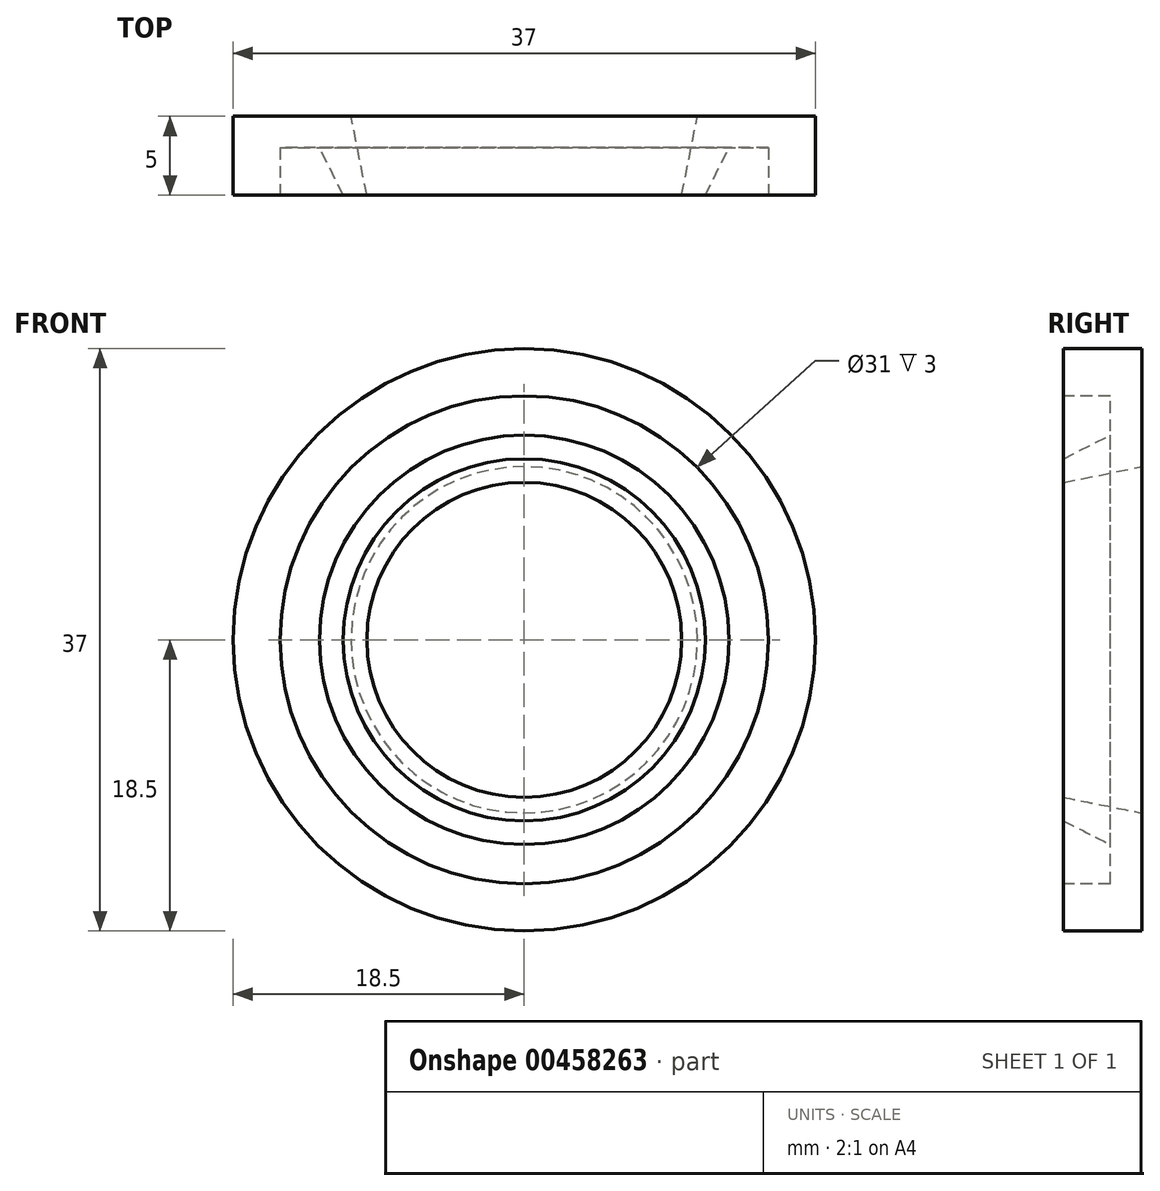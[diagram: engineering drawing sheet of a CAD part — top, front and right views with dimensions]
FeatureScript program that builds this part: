
annotation { "Feature Type Name" : "Feature", "Feature Type Description" : "" }
export const myFeature = defineFeature(function(context is Context, id is Id, definition is map)
    precondition{}
    {
        {
            var Q0;
            Q0=qCreatedBy(makeId("Right.planeOp"),FACE);
            var sketch = newSketch(context, id + "F0", { "sketchPlane" : qUnion([Q0])});
            skLineSegment(sketch, "E0", {"start": v(0, 18.5) * mm, "end": v(0, 11) * mm});
            skLineSegment(sketch, "E1", {"start": v(0, 11) * mm, "end": v(-5, 10) * mm});
            skLineSegment(sketch, "E2", {"start": v(-5, 10) * mm, "end": v(-5, 11.5) * mm});
            skLineSegment(sketch, "E3", {"start": v(-5, 11.5) * mm, "end": v(-2, 13) * mm});
            skLineSegment(sketch, "E4", {"start": v(-2, 13) * mm, "end": v(-2, 15.5) * mm});
            skLineSegment(sketch, "E5", {"start": v(-2, 15.5) * mm, "end": v(-5, 15.5) * mm});
            skLineSegment(sketch, "E6", {"start": v(-5, 15.5) * mm, "end": v(-5, 18.5) * mm});
            skLineSegment(sketch, "E7", {"start": v(-5, 18.5) * mm, "end": v(0, 18.5) * mm});
            skLineSegment(sketch, "E8", {"start": v(-9.9, 0) * mm, "end": v(14.4, 0) * mm, "construction": true});
            skSolve(sketch);
        }
        {
            var Q0;
            Q0=makeQuery(id+"F0.imprint","IMPRINT",FACE,{"disambiguationData":[TD([[makeQuery(id+"F0.imprint","IMPRINT",EDGE,{"derivedFrom":sQuery(id+"F0.wireOp",EDGE,"E0")}),-1.0]])]});
            var Q1;
            Q1=sQuery(id+"F0.wireOp",EDGE,"E8");
            revolve(context, id + "F1", {"entities" : qUnion([Q0]), "axis" : qUnion([Q1]), "revolveType" : RevolveType.FULL});
        }
    });
